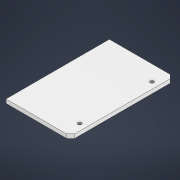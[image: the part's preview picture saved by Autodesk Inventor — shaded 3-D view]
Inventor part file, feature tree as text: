
AUTODESK INVENTOR PART (.ipt)
format: ipt  version: 2021 (Build 250183000, 183)  size: 105,472 bytes
history: native  units: mm
features: extrude x1, chamfer x1, sketch x1
ambient origin geometry x8: Origin, YZ Plane, XZ Plane, XY Plane, X Axis, Y Axis, Z Axis, Center Point
bodies: Solid1 (feature_tree)
feature tree (3):
  extrude  "Extrusion1"  Depth=3.0mm
  chamfer  "Chamfer1"  Distance=2.8mm
  sketch  "Sketch2"  dims[d2=160.0mm d3=90.0mm d4=2.8mm d5=5.0mm d6=5.0mm d8=3.0mm d9=0.0mm d10=28.0mm d11=50.0mm d12=3.0mm d13=2.0mm d14=45.0deg]
